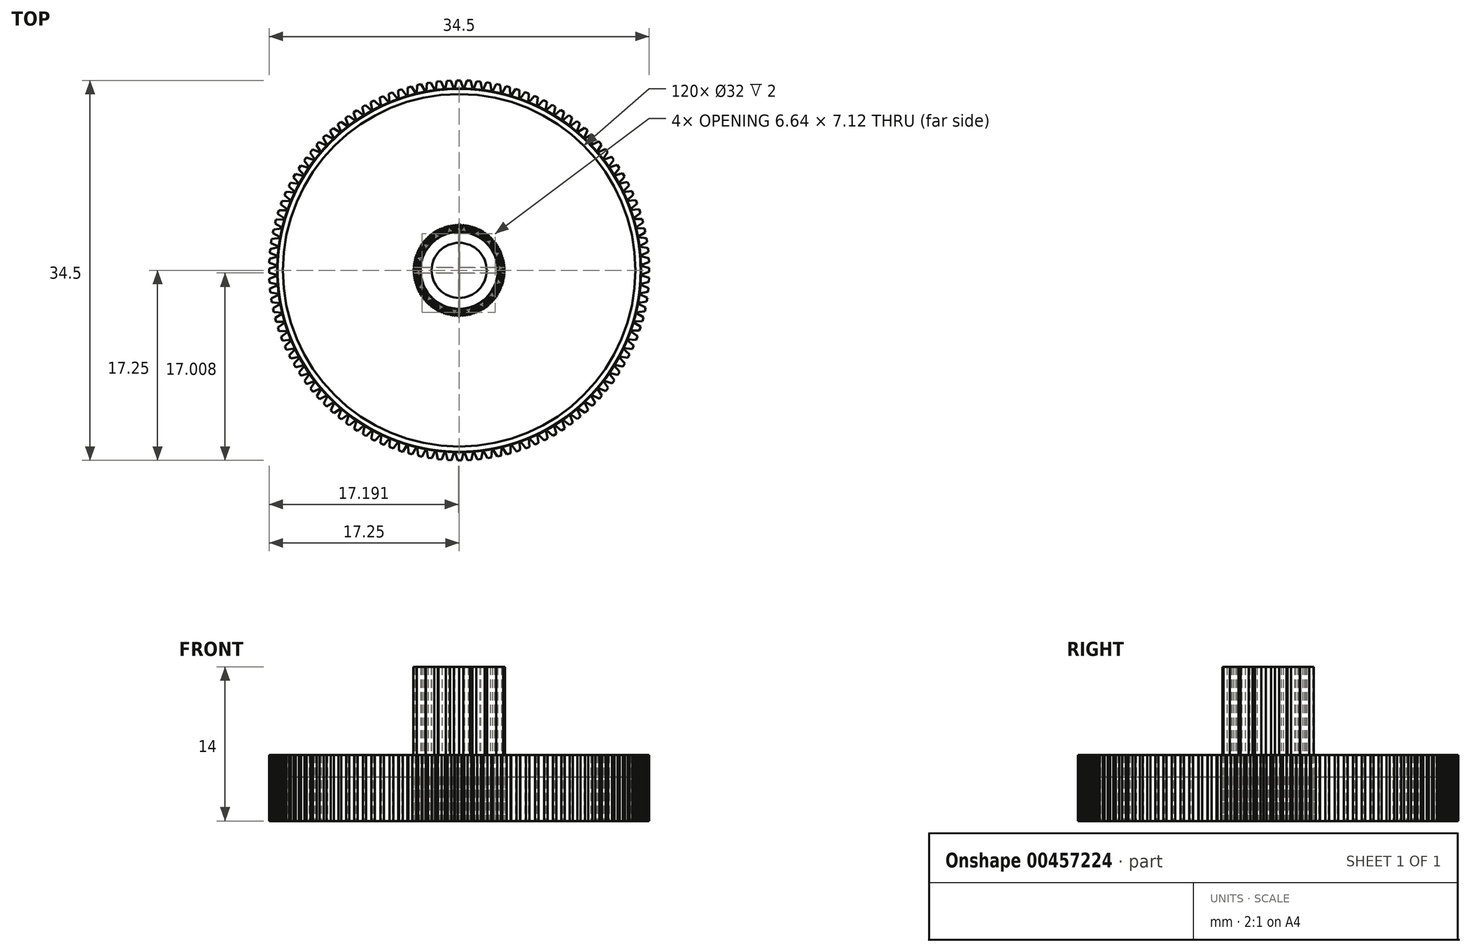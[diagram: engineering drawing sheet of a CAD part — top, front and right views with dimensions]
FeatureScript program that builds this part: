
annotation { "Feature Type Name" : "Feature", "Feature Type Description" : "" }
export const myFeature = defineFeature(function(context is Context, id is Id, definition is map)
    precondition{}
    {
        {
            var Q0;
            Q0=qCreatedBy(makeId("Top.planeOp"),FACE);
            var sketch = newSketch(context, id + "F0", { "sketchPlane" : qUnion([Q0])});
            skCircle(sketch, "E0", {"center": v(0, 0) * mm, "radius": 16.5 * mm});
            skCircle(sketch, "E1", {"center": v(0, 0) * mm, "radius": 16 * mm});
            skCircle(sketch, "E2", {"center": v(0, 0) * mm, "radius": 2.5 * mm});
            skCircle(sketch, "E3", {"center": v(0, 0) * mm, "radius": 3.5 * mm});
            skLineSegment(sketch, "E4", {"start": v(0, 3.5) * mm, "end": v(0.47, 4.15) * mm});
            skLineSegment(sketch, "E5", {"start": v(0.47, 4.15) * mm, "end": v(0.82, 3.4) * mm});
            skLineSegment(sketch, "E6", {"start": v(0.82, 3.4) * mm, "end": v(0, 3.5) * mm});
            skCircle(sketch, "E7", {"center": v(0, 0) * mm, "radius": 4.18 * mm, "construction": true});
            skLineSegment(sketch, "E8.1.0.0", {"start": v(25, 3.5) * mm, "end": v(25.47, 4.15) * mm});
            skLineSegment(sketch, "E8.1.0.1", {"start": v(25.47, 4.15) * mm, "end": v(25.82, 3.4) * mm});
            skLineSegment(sketch, "E8.1.0.2", {"start": v(25.82, 3.4) * mm, "end": v(25, 3.5) * mm});
            skLineSegment(sketch, "E8.2.0.0", {"start": v(50, 3.5) * mm, "end": v(50.47, 4.15) * mm});
            skLineSegment(sketch, "E8.2.0.1", {"start": v(50.47, 4.15) * mm, "end": v(50.82, 3.4) * mm});
            skLineSegment(sketch, "E8.2.0.2", {"start": v(50.82, 3.4) * mm, "end": v(50, 3.5) * mm});
            skLineSegment(sketch, "E8.direction1", {"start": v(0, 3.5) * mm, "end": v(25, 3.5) * mm, "construction": true});
            skCircle(sketch, "E9.1.0.3", {"center": v(25, 0) * mm, "radius": 3.5 * mm});
            skCircle(sketch, "E9.2.0.3", {"center": v(50, 0) * mm, "radius": 3.5 * mm});
            skCircle(sketch, "E10", {"center": v(0, 0) * mm, "radius": 17.25 * mm, "construction": true});
            skLineSegment(sketch, "E11", {"start": v(5.13, 16.47) * mm, "end": v(5.46, 16.36) * mm});
            skLineSegment(sketch, "E12", {"start": v(5.46, 16.36) * mm, "end": v(5.46, 15.57) * mm});
            skLineSegment(sketch, "E13", {"start": v(5.13, 16.47) * mm, "end": v(4.7, 15.82) * mm});
            skLineSegment(sketch, "E14", {"start": v(4.7, 15.82) * mm, "end": v(5.46, 15.57) * mm});
            skSolve(sketch);
        }
        {
            var Q0;
            Q0=makeQuery(id+"F0.imprint","IMPRINT",FACE,{"disambiguationData":[TD([[makeQuery(id+"F0.imprint","IMPRINT",EDGE,{"derivedFrom":sQuery(id+"F0.wireOp",EDGE,"E2")}),-1.0]])]});
            var Q1;
            {var subQ1=sQuery(id+"F0.wireOp",EDGE,"E4");Q1=makeQuery(id+"F0.imprint","IMPRINT",FACE,{"disambiguationData":[TD([[makeQuery(id+"F0.imprint","IMPRINT",EDGE,{"derivedFrom":subQ1}),-1.0]])]});}
            extrude(context, id + "F1", {"entities" : qUnion([Q0, Q1]), "depth" : 14 * mm});
        }
        {
            var Q0;
            Q0=makeQuery(id+"F1.opExtrude","SWEPT_BODY",BODY,{"disambiguationData":[OSD([sQuery(id+"F0.wireOp",EDGE,"E3"),sQuery(id+"F0.wireOp",EDGE,"E4"),sQuery(id+"F0.wireOp",EDGE,"E5")])]});
            var Q1;
            Q1=makeQuery(id+"F1.opExtrude","CAP_EDGE",EDGE,{"disambiguationData":[OSD([sQuery(id+"F0.wireOp",EDGE,"E2")])],"isStart":false});
            circularPattern(context, id + "F2", {"entities" : qUnion([Q0]), "axis" : qUnion([Q1]), "angle" : 360 * degree, "instanceCount" : 18, "equalSpace" : true});
        }
        {
            var Q0;
            Q0=makeQuery(id+"F0.imprint","IMPRINT",FACE,{"disambiguationData":[TD([[makeQuery(id+"F0.imprint","IMPRINT",EDGE,{"derivedFrom":sQuery(id+"F0.wireOp",EDGE,"E1")}),1.0]])]});
            extrude(context, id + "F3", {"entities" : qUnion([Q0]), "depth" : 4 * mm});
        }
        {
            var Q0;
            Q0=makeQuery(id+"F0.imprint","IMPRINT",FACE,{"disambiguationData":[TD([[makeQuery(id+"F0.imprint","IMPRINT",EDGE,{"derivedFrom":sQuery(id+"F0.wireOp",EDGE,"E1")}),-1.0]])]});
            var Q1;
            Q1=makeQuery(id+"F0.imprint","IMPRINT",FACE,{"disambiguationData":[TD([[makeQuery(id+"F0.imprint","IMPRINT",EDGE,{"derivedFrom":sQuery(id+"F0.wireOp",EDGE,"E11")}),-1.0]])]});
            extrude(context, id + "F4", {"entities" : qUnion([Q0, Q1]), "operationType" : NewBodyOperationType.ADD, "depth" : 6 * mm});
        }
        {
            var Q0;
            Q0=makeQuery(id+"F3.opExtrude","SWEPT_BODY",BODY,{"disambiguationData":[OSD([sQuery(id+"F0.wireOp",EDGE,"E1"),sQuery(id+"F0.wireOp",EDGE,"E3"),sQuery(id+"F0.wireOp",EDGE,"E4"),sQuery(id+"F0.wireOp",EDGE,"E5")])]});
            var Q1;
            Q1=sQuery(id+"F0.wireOp",EDGE,"E1");
            circularPattern(context, id + "F5", {"entities" : qUnion([Q0]), "axis" : qUnion([Q1]), "angle" : 360 * degree, "instanceCount" : 120, "equalSpace" : true});
        }
    });
